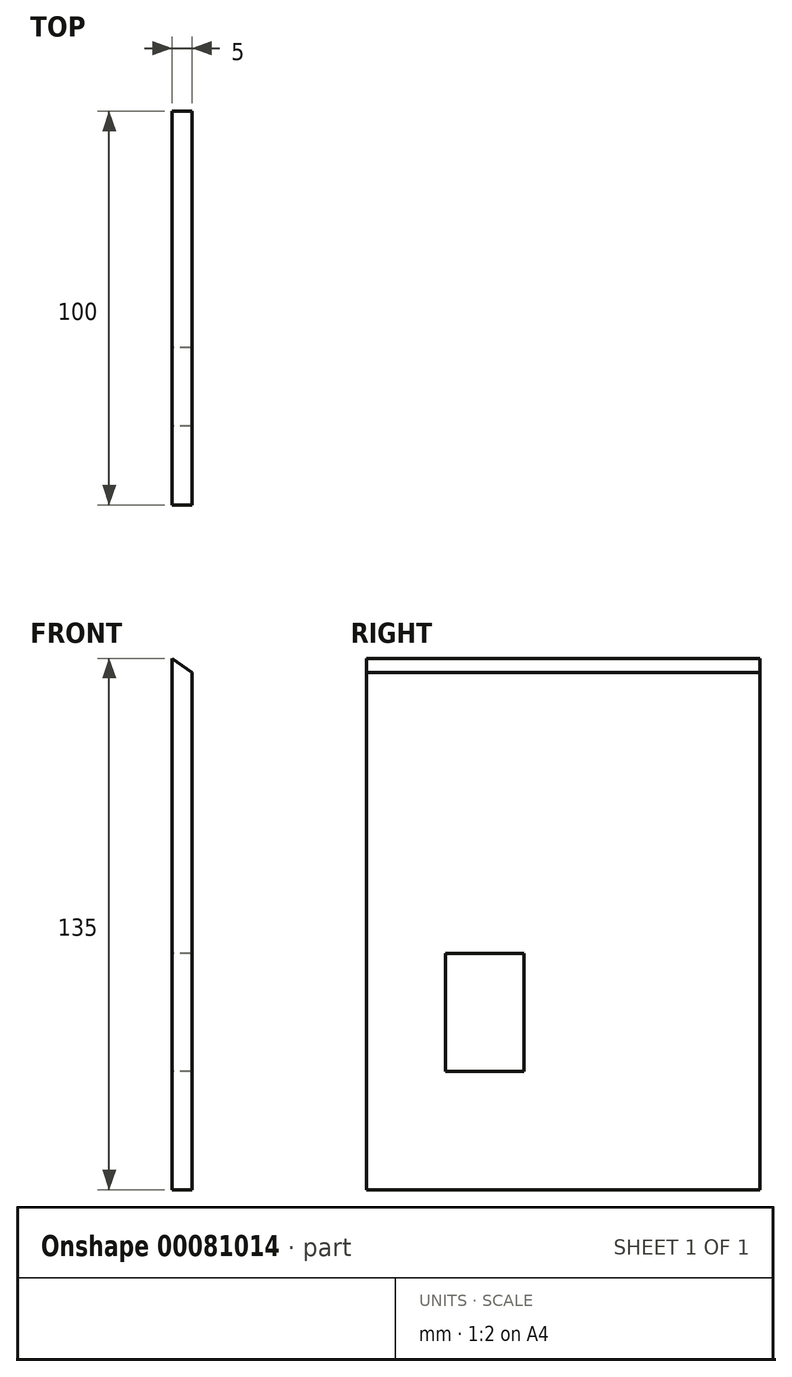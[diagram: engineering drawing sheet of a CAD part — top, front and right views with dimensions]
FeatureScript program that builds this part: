
annotation { "Feature Type Name" : "Feature", "Feature Type Description" : "" }
export const myFeature = defineFeature(function(context is Context, id is Id, definition is map)
    precondition{}
    {
        {
            var Q0;
            Q0=qCreatedBy(makeId("Right.planeOp"),FACE);
            var sketch = newSketch(context, id + "F0", { "sketchPlane" : qUnion([Q0])});
            skLineSegment(sketch, "E0.bottom", {"start": v(-100, 130) * mm, "end": v(0, 130) * mm});
            skLineSegment(sketch, "E0.top", {"start": v(-100, 0) * mm, "end": v(0, 0) * mm});
            skLineSegment(sketch, "E0.left", {"start": v(-100, 130) * mm, "end": v(-100, 0) * mm});
            skLineSegment(sketch, "E0.right", {"start": v(0, 130) * mm, "end": v(0, 0) * mm});
            skPoint(sketch, "E1", {"position": v(0, 80) * mm});
            skLineSegment(sketch, "E2", {"start": v(0, 80) * mm, "end": v(-100, 80) * mm});
            skLineSegment(sketch, "E3.bottom", {"start": v(-80, 55) * mm, "end": v(-60, 55) * mm});
            skLineSegment(sketch, "E3.top", {"start": v(-80, 25) * mm, "end": v(-60, 25) * mm});
            skLineSegment(sketch, "E3.left", {"start": v(-80, 55) * mm, "end": v(-80, 25) * mm});
            skLineSegment(sketch, "E3.right", {"start": v(-60, 55) * mm, "end": v(-60, 25) * mm});
            skLineSegment(sketch, "E4", {"start": v(0, 0) * mm, "end": v(0, -5) * mm});
            skLineSegment(sketch, "E5", {"start": v(0, -5) * mm, "end": v(-100, -5) * mm});
            skLineSegment(sketch, "E6", {"start": v(-100, -5) * mm, "end": v(-100, 0) * mm});
            skSolve(sketch);
        }
        {
            var Q0;
            {var subQ2=sQuery(id+"F0.wireOp",EDGE,"E0.top");Q0=makeQuery(id+"F0.imprint","IMPRINT",FACE,{"disambiguationData":[TD([[makeQuery(id+"F0.imprint","IMPRINT",EDGE,{"derivedFrom":subQ2}),1.0]])]});}
            var Q1;
            {var subQ2=sQuery(id+"F0.wireOp",EDGE,"E0.bottom");Q1=makeQuery(id+"F0.imprint","IMPRINT",FACE,{"disambiguationData":[TD([[makeQuery(id+"F0.imprint","IMPRINT",EDGE,{"derivedFrom":subQ2}),-1.0]])]});}
            var Q2;
            Q2=makeQuery(id+"F0.imprint","IMPRINT",FACE,{"disambiguationData":[TD([[makeQuery(id+"F0.imprint","IMPRINT",EDGE,{"derivedFrom":sQuery(id+"F0.wireOp",EDGE,"E0.top")}),-1.0]])]});
            extrude(context, id + "F1", {"entities" : qUnion([Q0, Q1, Q2]), "endBound" : BoundingType.SYMMETRIC, "depth" : 5 * mm});
        }
        {
            var Q0;
            Q0=makeQuery(id+"F1.opExtrude","CAP_EDGE",EDGE,{"disambiguationData":[OSD([sQuery(id+"F0.wireOp",EDGE,"E0.bottom")])],"isStart":false});
            chamfer(context, id + "F2", {"entities" : qUnion([Q0]), "chamferType" : ChamferType.OFFSET_ANGLE, "width" : 5 * mm, "oppositeDirection" : false, "angle" : 35.53 * degree, "tangentPropagation" : true});
        }
    });
